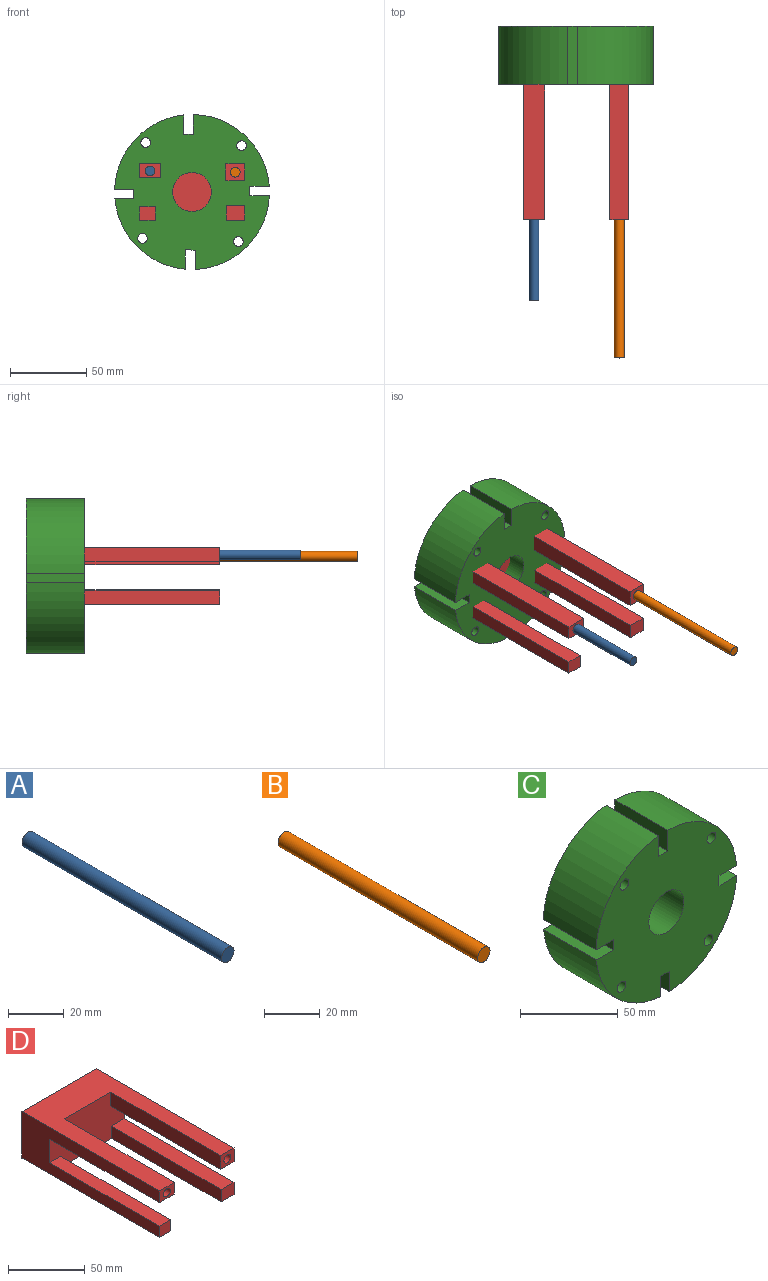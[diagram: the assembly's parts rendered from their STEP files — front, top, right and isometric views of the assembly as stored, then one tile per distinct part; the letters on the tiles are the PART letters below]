
ASSEMBLY  parts=4 mates=3
PART A: 3 faces, bbox 6.4x101.6x6.4 mm
  f0: cylinder r=3.17mm len=101.6mm, axis (0,1,0), area 2026.8mm2, adj f1,f2
  f1: plane 6.35x6.35mm, normal (0,-1,0), area 31.7mm2, adj f0
  f2: plane 6.35x6.35mm, normal (0,1,0), area 31.7mm2, adj f0
PART B: 3 faces, bbox 6.4x101.6x6.4 mm
  f0: cylinder r=3.17mm len=101.6mm, axis (0,1,0), area 2026.8mm2, adj f1,f2
  f1: plane 6.35x6.35mm, normal (0,-1,0), area 31.7mm2, adj f0
  f2: plane 6.35x6.35mm, normal (0,1,0), area 31.7mm2, adj f0
PART C: 23 faces, bbox 101.5x38.1x101.6 mm
  f0: plane 38.1x12.7mm, normal (1,0,0), area 483.9mm2, adj f1,f19,f21,f22
  f1: cylinder r=50.8mm len=48.72mm, axis (0,1,0), area 2763.6mm2, adj f0,f2,f21,f22
  f2: plane 38.1x12.7mm, normal (0,0,-1), area 483.9mm2, adj f1,f3,f21,f22
  f3: plane 38.1x6.35mm, normal (-1,0,0), area 241.9mm2, adj f2,f4,f21,f22
  f4: plane 38.1x12.53mm, normal (0,0,1), area 477.2mm2, adj f3,f5,f21,f22
  f5: cylinder r=50.8mm len=46.31mm, axis (0,1,0), area 2702.6mm2, adj f4,f6,f21,f22
  f6: plane 38.1x12.7mm, normal (1,0,0), area 483.9mm2, adj f5,f7,f21,f22
  f7: plane 38.1x6.35mm, normal (-0.02,0,-1), area 241.9mm2, adj f6,f8,f21,f22
  f8: plane 38.1x12.7mm, normal (-1,0,0), area 483.9mm2, adj f7,f9,f21,f22
  f9: cylinder r=50.8mm len=48.68mm, axis (0,1,0), area 2867.4mm2, adj f8,f10,f21,f22
  f10: plane 38.1x12.79mm, normal (0,0,1), area 487.2mm2, adj f9,f11,f21,f22
  f11: plane 38.1x6.35mm, normal (1,0,0), area 241.9mm2, adj f10,f12,f21,f22
  f12: plane 38.1x12.7mm, normal (0,0,-1), area 483.9mm2, adj f11,f13,f21,f22
  f13: cylinder r=50.8mm len=49.77mm, axis (0,1,0), area 2858.7mm2, adj f12,f14,f21,f22
  f14: plane 38.1x12.99mm, normal (-1,0,0), area 494.8mm2, adj f13,f19,f21,f22
  f15: cylinder r=3.17mm len=38.1mm, axis (0,1,0), area 760.1mm2, adj f21,f22
  f16: cylinder r=3.17mm len=38.1mm, axis (0,1,0), area 760.1mm2, adj f21,f22
  f17: cylinder r=3.17mm len=38.1mm, axis (0,1,0), area 760.1mm2, adj f21,f22
  f18: cylinder r=3.17mm len=38.1mm, axis (0,1,0), area 760.1mm2, adj f21,f22
  f19: plane 38.1x6.35mm, normal (0,0,1), area 241.9mm2, adj f0,f14,f21,f22
  f20: cylinder r=12.7mm len=38.1mm, axis (0,1,0), area 3040.2mm2, adj f21,f22
  f21: plane 101.55x101.51mm, normal (0,-1,0), area 7149.1mm2, adj f0,f1,f2,f3,f4,f5,f6,f7
  f22: plane 101.55x101.51mm, normal (0,1,0), area 7149.1mm2, adj f0,f1,f2,f3,f4,f5,f6,f7
PART D: 22 faces, bbox 68.8x127x37.1 mm
  f0: plane 127x68.83mm, normal (0,0,-1), area 4000.3mm2, adj f1,f3,f4,f5,f13,f14,f15,f17
  f1: plane 127x37.14mm, normal (1,0,0), area 3057mm2, adj f0,f2,f4,f5,f10,f11,f12,f14
  f2: plane 127x68.83mm, normal (0,0,1), area 4395.4mm2, adj f1,f3,f4,f5,f6,f8,f9,f11
  f3: plane 127x37.14mm, normal (-1,0,0), area 2800.2mm2, adj f0,f2,f4,f5,f7,f8,f16,f17
  f4: plane 68.83x37.14mm, normal (0,-1,0), area 2084.1mm2, adj f0,f1,f2,f3,f6,f7,f9,f10
  f5: plane 68.83x37.14mm, normal (0,1,0), area 2556.1mm2, adj f0,f1,f2,f3
  f6: plane 101.6x9.33mm, normal (1,0,0), area 948.2mm2, adj f2,f4,f7,f8
  f7: plane 101.6x13.81mm, normal (0,0,-1), area 1402.6mm2, adj f3,f4,f6,f8
  f8: plane 13.81x9.33mm, normal (0,-1,0), area 97.2mm2, adj f2,f3,f6,f7,f18
  f9: plane 101.6x11.08mm, normal (-1,0,0), area 1126mm2, adj f2,f4,f10,f11
  f10: plane 101.6x12.25mm, normal (0,0,-1), area 1244.5mm2, adj f1,f4,f9,f11
  f11: plane 12.25x11.08mm, normal (0,-1,0), area 104.1mm2, adj f1,f2,f9,f10,f20
  f12: plane 101.6x11.86mm, normal (0,0,1), area 1205mm2, adj f1,f4,f13,f14
  f13: plane 101.6x9.72mm, normal (-1,0,0), area 987.7mm2, adj f0,f4,f12,f14
  f14: plane 11.86x9.72mm, normal (0,-1,0), area 115.3mm2, adj f0,f1,f12,f13
  f15: plane 101.6x8.94mm, normal (1,0,0), area 908.7mm2, adj f0,f4,f16,f17
  f16: plane 101.6x10.31mm, normal (0,0,1), area 1047mm2, adj f3,f4,f15,f17
  f17: plane 10.31x8.94mm, normal (0,-1,0), area 92.2mm2, adj f0,f3,f15,f16
  f18: cylinder r=3.17mm len=101.6mm, axis (0,-1,0), area 2026.8mm2, adj f8,f19
  f19: plane 6.35x6.35mm, normal (0,-1,0), area 31.7mm2, adj f18
  f20: cylinder r=3.17mm len=101.6mm, axis (0,-1,0), area 2026.8mm2, adj f11,f21
  f21: plane 6.35x6.35mm, normal (0,-1,0), area 31.7mm2, adj f20
PLACE A t=(-87.01,-124.77,-1.01)mm
PLACE B t=(-41.77,-162.48,1.73)mm
PLACE C t=(-97.9,-46.53,23.6)mm
PLACE D t=(-63.45,-46.53,42.17)mm
MATE slider A.f0 <-> D.f18  axis (0,1,0) through (-125.37,-175.57,37.47)mm
MATE fastened D.f5 <-> C.f22  axis (0,1,0) through (-97.86,-46.53,23.6)mm
MATE slider B.f0 <-> D.f20  axis (0,1,0) through (-69.57,-213.28,36.53)mm
